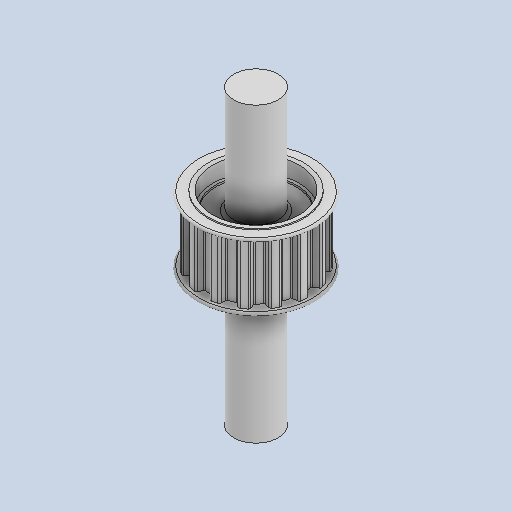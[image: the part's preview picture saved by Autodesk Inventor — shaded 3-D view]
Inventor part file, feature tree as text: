
AUTODESK INVENTOR PART (.ipt)
format: ipt  version: 2022 (Build 260153000, 153)  size: 303,104 bytes
history: native  units: in
note: dims shown in document units (in); Inventor stores cm internally (conversion verified against a paired STEP export)
features: fillet x1
ambient origin geometry x8: Origin, YZ Plane, XZ Plane, XY Plane, X Axis, Y Axis, Z Axis, Center Point
bodies: Solid1 (feature_tree)
feature tree (1):
  fillet  "Fillet1"  [1 undecoded]
note: 1 required parameter value undecoded (feature->parameter linkage not recoverable at this tier; creation-order binding heuristic only, values carry confidence <= 0.55)
